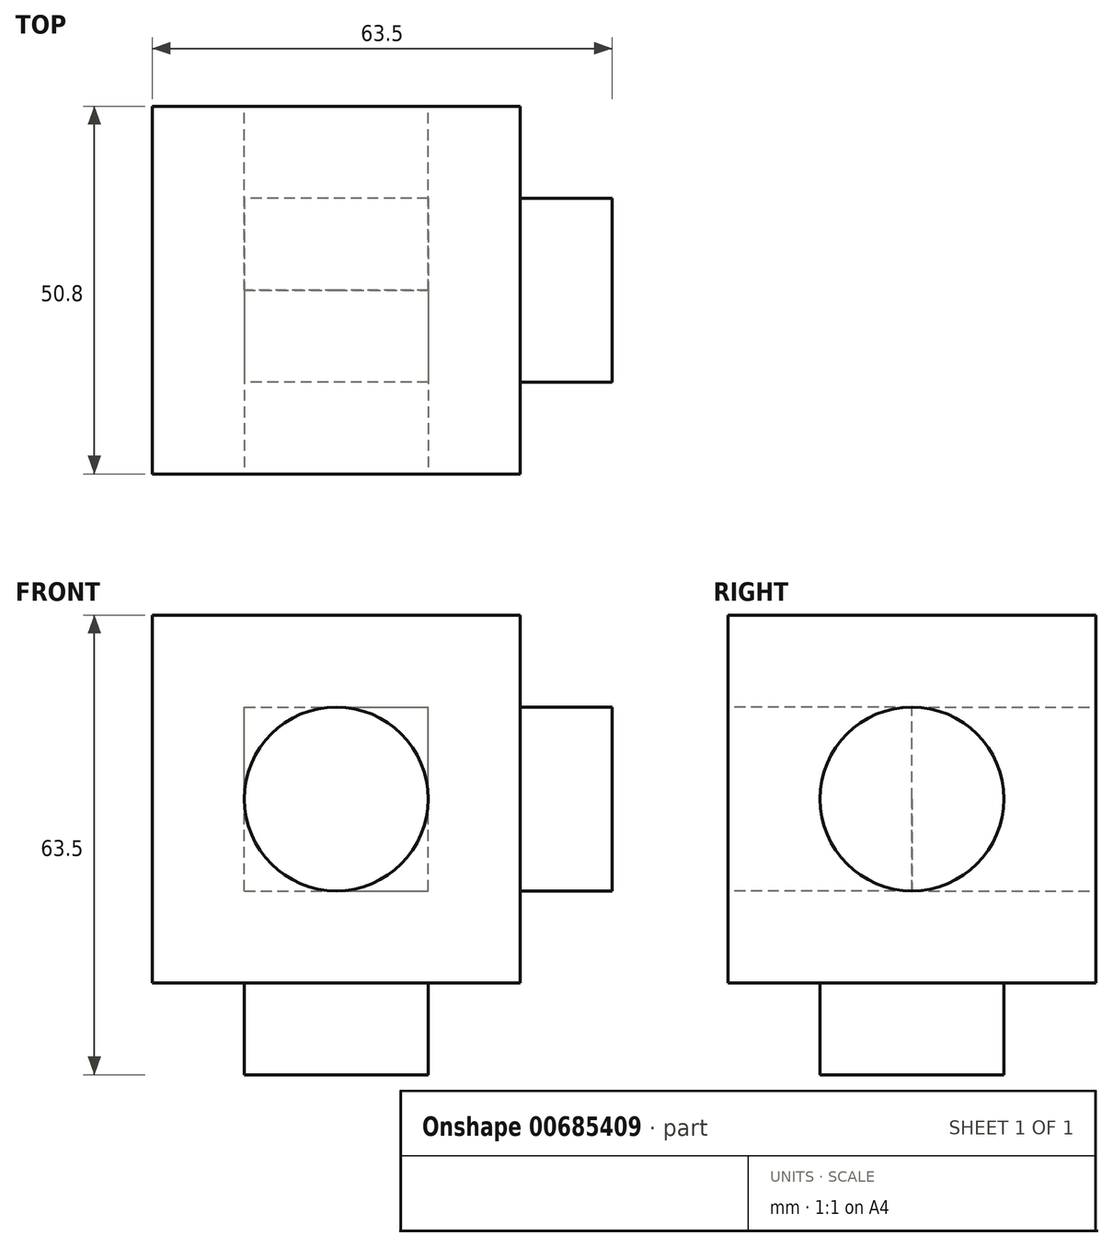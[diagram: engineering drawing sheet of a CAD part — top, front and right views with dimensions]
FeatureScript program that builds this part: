
annotation { "Feature Type Name" : "Feature", "Feature Type Description" : "" }
export const myFeature = defineFeature(function(context is Context, id is Id, definition is map)
    precondition{}
    {
        {
            var Q0;
            Q0=qCreatedBy(makeId("Front.planeOp"),FACE);
            var sketch = newSketch(context, id + "F0", { "sketchPlane" : qUnion([Q0])});
            skLineSegment(sketch, "E0", {"start": v(0, 0) * mm, "end": v(-50.8, 0) * mm});
            skLineSegment(sketch, "E1", {"start": v(-50.8, 0) * mm, "end": v(-50.8, 50.8) * mm});
            skLineSegment(sketch, "E2", {"start": v(-50.8, 50.8) * mm, "end": v(0, 50.8) * mm});
            skLineSegment(sketch, "E3", {"start": v(0, 50.8) * mm, "end": v(0, 0) * mm});
            skSolve(sketch);
        }
        {
            var Q0;
            Q0 = qSketchRegion(id + "F0", true);
            extrude(context, id + "F1", {"entities" : qUnion([Q0]), "depth" : 50.8 * mm, "offsetDistance" : 25.4 * mm});
        }
        {
            var Q0;
            Q0=makeQuery(id+"F1.opExtrude","CAP_FACE",FACE,{"disambiguationData":[OSD([sQuery(id+"F0.wireOp",EDGE,"E0"),sQuery(id+"F0.wireOp",EDGE,"E1"),sQuery(id+"F0.wireOp",EDGE,"E2"),sQuery(id+"F0.wireOp",EDGE,"E3")])],"isStart":false});
            var sketch = newSketch(context, id + "F2", { "sketchPlane" : qUnion([Q0])});
            skCircle(sketch, "E4", {"center": v(-25.4, 25.4) * mm, "radius": 12.7 * mm});
            skSolve(sketch);
        }
        {
            var Q0;
            Q0 = qSketchRegion(id + "F2", true);
            extrude(context, id + "F3", {"entities" : qUnion([Q0]), "operationType" : NewBodyOperationType.REMOVE, "oppositeDirection" : true, "depth" : 25.4 * mm, "offsetDistance" : 25.4 * mm});
        }
        {
            var Q0;
            Q0=makeQuery(id+"F1.opExtrude","SWEPT_FACE",FACE,{"disambiguationData":[OSD([sQuery(id+"F0.wireOp",EDGE,"E3")])]});
            var sketch = newSketch(context, id + "F4", { "sketchPlane" : qUnion([Q0])});
            skCircle(sketch, "E5", {"center": v(-25.4, 25.4) * mm, "radius": 12.7 * mm});
            skSolve(sketch);
        }
        {
            var Q0;
            Q0 = qSketchRegion(id + "F4", true);
            extrude(context, id + "F5", {"entities" : qUnion([Q0]), "operationType" : NewBodyOperationType.ADD, "depth" : 12.7 * mm, "offsetDistance" : 25.4 * mm});
        }
        {
            var Q0;
            Q0=makeQuery(id+"F1.opExtrude","SWEPT_FACE",FACE,{"disambiguationData":[OSD([sQuery(id+"F0.wireOp",EDGE,"E0")])]});
            var sketch = newSketch(context, id + "F6", { "sketchPlane" : qUnion([Q0])});
            skLineSegment(sketch, "E6.bottom", {"start": v(-12.7, 12.7) * mm, "end": v(-38.1, 12.7) * mm});
            skLineSegment(sketch, "E6.top", {"start": v(-12.7, 38.1) * mm, "end": v(-38.1, 38.1) * mm});
            skLineSegment(sketch, "E6.left", {"start": v(-12.7, 12.7) * mm, "end": v(-12.7, 38.1) * mm});
            skLineSegment(sketch, "E6.right", {"start": v(-38.1, 12.7) * mm, "end": v(-38.1, 38.1) * mm});
            skPoint(sketch, "E6.middle", {"position": v(-25.4, 25.4) * mm});
            skSolve(sketch);
        }
        {
            var Q0;
            Q0=makeQuery(id+"F6.imprint","IMPRINT",FACE,{"disambiguationData":[TD([[makeQuery(id+"F6.imprint","IMPRINT",EDGE,{"derivedFrom":sQuery(id+"F6.wireOp",EDGE,"E6.bottom")}),-1.0]])]});
            extrude(context, id + "F7", {"entities" : qUnion([Q0]), "operationType" : NewBodyOperationType.ADD, "depth" : 12.7 * mm, "offsetDistance" : 25.4 * mm});
        }
        {
            var Q0;
            Q0=makeQuery(id+"F1.opExtrude","CAP_FACE",FACE,{"disambiguationData":[OSD([sQuery(id+"F0.wireOp",EDGE,"E0"),sQuery(id+"F0.wireOp",EDGE,"E1"),sQuery(id+"F0.wireOp",EDGE,"E2"),sQuery(id+"F0.wireOp",EDGE,"E3")])],"isStart":true});
            var sketch = newSketch(context, id + "F8", { "sketchPlane" : qUnion([Q0])});
            skLineSegment(sketch, "E7.bottom", {"start": v(38.1, 12.7) * mm, "end": v(12.7, 12.7) * mm});
            skLineSegment(sketch, "E7.top", {"start": v(38.1, 38.1) * mm, "end": v(12.7, 38.1) * mm});
            skLineSegment(sketch, "E7.left", {"start": v(38.1, 12.7) * mm, "end": v(38.1, 38.1) * mm});
            skLineSegment(sketch, "E7.right", {"start": v(12.7, 12.7) * mm, "end": v(12.7, 38.1) * mm});
            skPoint(sketch, "E7.middle", {"position": v(25.4, 25.4) * mm});
            skSolve(sketch);
        }
        {
            var Q0;
            Q0=makeQuery(id+"F8.imprint","IMPRINT",FACE,{"disambiguationData":[TD([[makeQuery(id+"F8.imprint","IMPRINT",EDGE,{"derivedFrom":sQuery(id+"F8.wireOp",EDGE,"E7.bottom")}),-1.0]])]});
            extrude(context, id + "F9", {"entities" : qUnion([Q0]), "operationType" : NewBodyOperationType.REMOVE, "oppositeDirection" : true, "depth" : 25.4 * mm, "offsetDistance" : 25.4 * mm});
        }
    });
